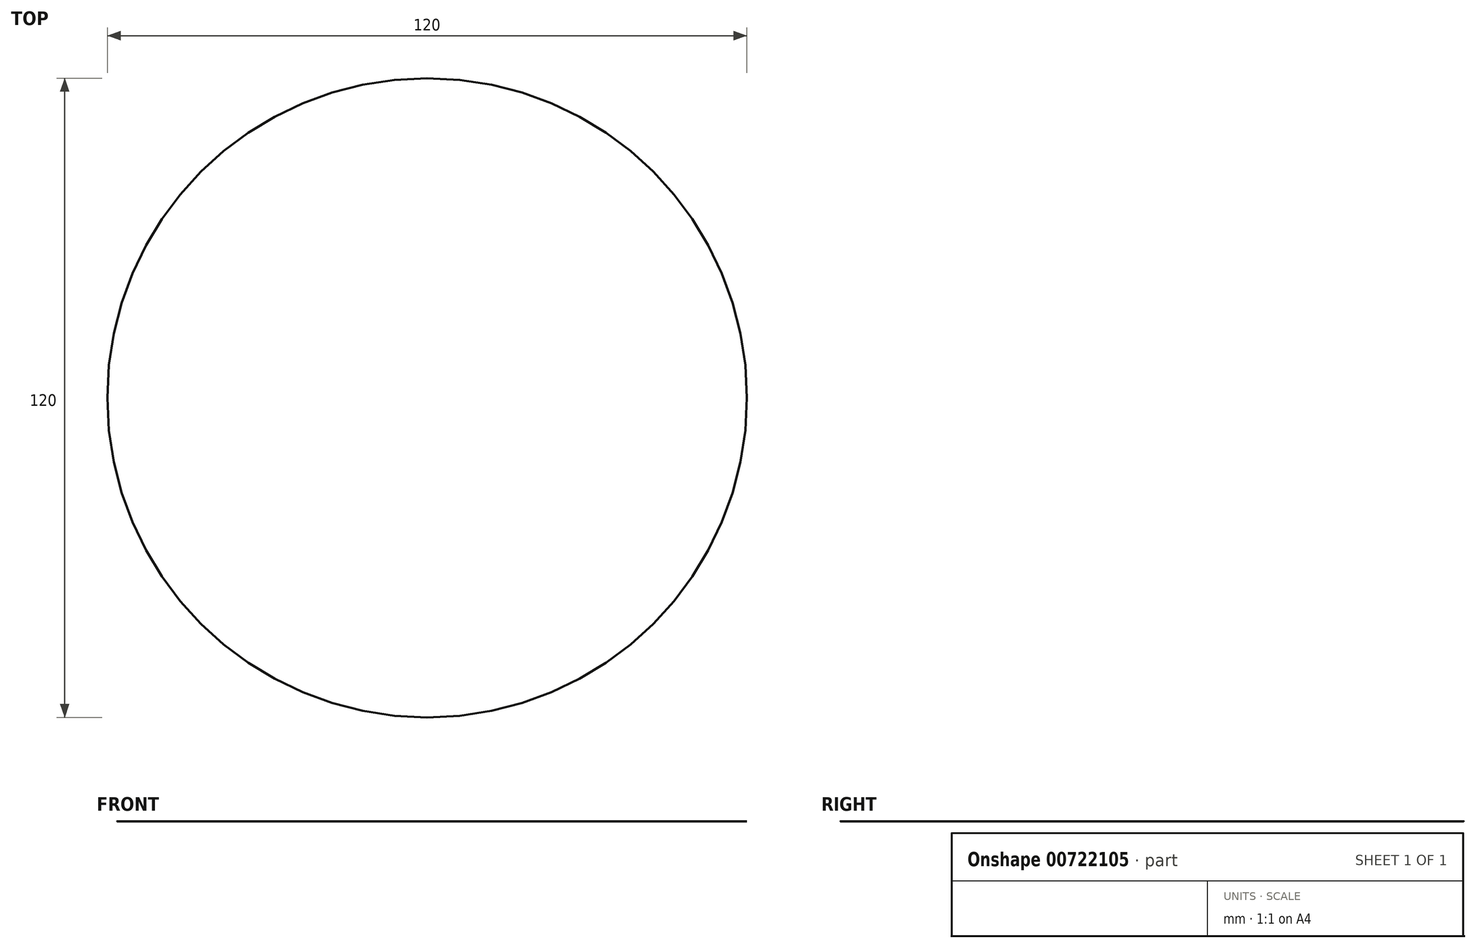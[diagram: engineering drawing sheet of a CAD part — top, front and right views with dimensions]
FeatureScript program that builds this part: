
annotation { "Feature Type Name" : "Feature", "Feature Type Description" : "" }
export const myFeature = defineFeature(function(context is Context, id is Id, definition is map)
    precondition{}
    {
        {
            var Q0;
            Q0=qCreatedBy(makeId("Front.planeOp"),FACE);
            var sketch = newSketch(context, id + "F0", { "sketchPlane" : qUnion([Q0])});
            skLineSegment(sketch, "E0.bottom", {"start": v(0, 0) * mm, "end": v(60, 0) * mm});
            skLineSegment(sketch, "E0.top", {"start": v(0, 2) * mm, "end": v(60, 2) * mm});
            skLineSegment(sketch, "E0.left", {"start": v(0, 0) * mm, "end": v(0, 2) * mm});
            skLineSegment(sketch, "E0.right", {"start": v(60, 0) * mm, "end": v(60, 2) * mm});
            skSolve(sketch);
        }
        {
            var Q0;
            Q0=sQuery(id+"F0.wireOp",EDGE,"E0.bottom");
            var Q1;
            Q1=sQuery(id+"F0.wireOp",EDGE,"E0.right");
            revolve(context, id + "F1", {"bodyType" : ToolBodyType.SURFACE, "surfaceOperationType" : NewSurfaceOperationType.NEW, "surfaceEntities" : qUnion([Q0]), "axis" : qUnion([Q1]), "revolveType" : RevolveType.FULL});
        }
    });
